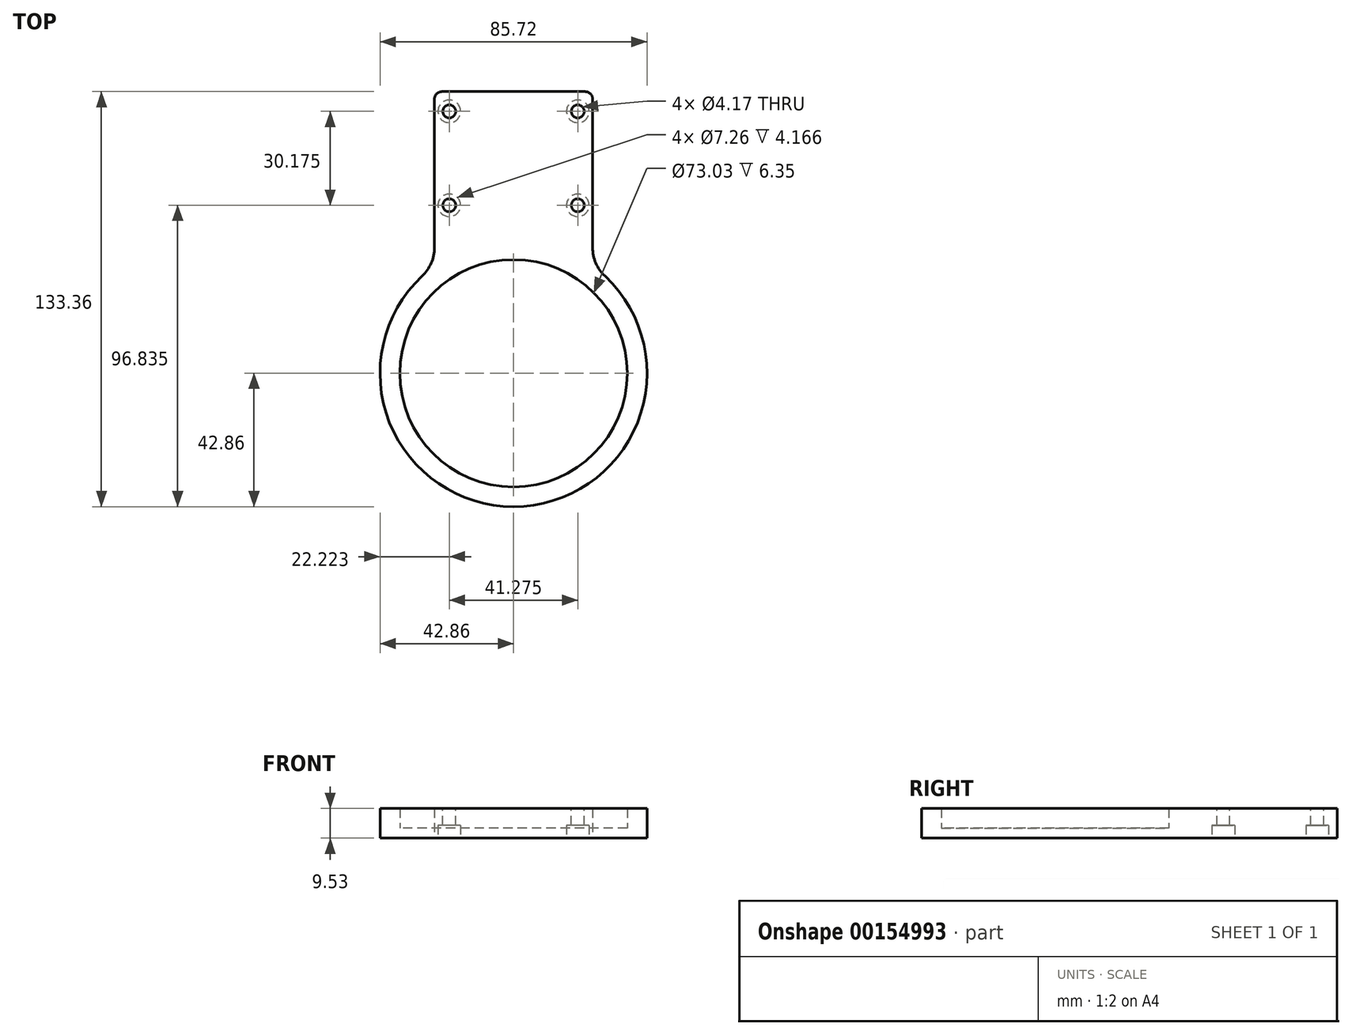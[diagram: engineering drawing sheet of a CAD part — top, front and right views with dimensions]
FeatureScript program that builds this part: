
annotation { "Feature Type Name" : "Feature", "Feature Type Description" : "" }
export const myFeature = defineFeature(function(context is Context, id is Id, definition is map)
    precondition{}
    {
        {
            var Q0;
            Q0=qCreatedBy(makeId("Top.planeOp"),FACE);
            var sketch = newSketch(context, id + "F0", { "sketchPlane" : qUnion([Q0])});
            skCircle(sketch, "E0", {"center": v(0, 0) * mm, "radius": 36.51 * mm});
            skArc(sketch, "E1", {"start": v(-25.4, 34.53) * mm, "mid": v(0, -42.86) * mm, "end": v(25.4, 34.53) * mm});
            skLineSegment(sketch, "E2", {"start": v(-25.4, 34.53) * mm, "end": v(-25.4, 90.5) * mm});
            skLineSegment(sketch, "E3", {"start": v(-25.4, 90.5) * mm, "end": v(25.4, 90.5) * mm});
            skLineSegment(sketch, "E4", {"start": v(25.4, 90.5) * mm, "end": v(25.4, 34.53) * mm});
            skLineSegment(sketch, "E5", {"start": v(0, 143.03) * mm, "end": v(0, 0) * mm, "construction": true});
            skSolve(sketch);
        }
        {
            var Q0;
            Q0=makeQuery(id+"F0.imprint","IMPRINT",FACE,{"disambiguationData":[TD([[makeQuery(id+"F0.imprint","IMPRINT",EDGE,{"derivedFrom":sQuery(id+"F0.wireOp",EDGE,"E0")}),-1.0]])]});
            extrude(context, id + "F1", {"entities" : qUnion([Q0]), "depth" : 9.52 * mm});
        }
        {
            var Q0;
            Q0=qCreatedBy(makeId("Top.planeOp"),FACE);
            var sketch = newSketch(context, id + "F2", { "sketchPlane" : qUnion([Q0])});
            skCircle(sketch, "E6", {"center": v(0, 0) * mm, "radius": 36.51 * mm});
            skSolve(sketch);
        }
        {
            var Q0;
            Q0 = qSketchRegion(id + "F2", true);
            extrude(context, id + "F3", {"entities" : qUnion([Q0]), "operationType" : NewBodyOperationType.ADD, "depth" : 3.17 * mm});
        }
        {
            var Q0;
            Q0=makeQuery(id+"F1.opExtrude","CAP_FACE",FACE,{"disambiguationData":[OSD([sQuery(id+"F0.wireOp",EDGE,"E0"),sQuery(id+"F0.wireOp",EDGE,"E1"),sQuery(id+"F0.wireOp",EDGE,"E2"),sQuery(id+"F0.wireOp",EDGE,"E3"),sQuery(id+"F0.wireOp",EDGE,"E4")])],"isStart":false});
            var sketch = newSketch(context, id + "F4", { "sketchPlane" : qUnion([Q0])});
            skLineSegment(sketch, "E7.bottom", {"start": v(-20.64, 84.15) * mm, "end": v(20.64, 84.15) * mm, "construction": true});
            skLineSegment(sketch, "E7.top", {"start": v(-20.64, 53.98) * mm, "end": v(20.64, 53.98) * mm, "construction": true});
            skLineSegment(sketch, "E7.left", {"start": v(-20.64, 84.15) * mm, "end": v(-20.64, 53.98) * mm, "construction": true});
            skLineSegment(sketch, "E7.right", {"start": v(20.64, 84.15) * mm, "end": v(20.64, 53.98) * mm, "construction": true});
            skCircle(sketch, "E8", {"center": v(-20.64, 84.15) * mm, "radius": 2.08 * mm});
            skCircle(sketch, "E9", {"center": v(20.64, 84.15) * mm, "radius": 2.08 * mm});
            skCircle(sketch, "E10", {"center": v(-20.64, 53.98) * mm, "radius": 2.08 * mm});
            skCircle(sketch, "E11", {"center": v(20.64, 53.98) * mm, "radius": 2.08 * mm});
            skSolve(sketch);
        }
        {
            var Q0;
            Q0 = qSketchRegion(id + "F4", true);
            extrude(context, id + "F5", {"entities" : qUnion([Q0]), "operationType" : NewBodyOperationType.REMOVE, "endBound" : BoundingType.THROUGH_ALL, "oppositeDirection" : true, "depth" : 25.4 * mm});
        }
        {
            var Q0;
            Q0=makeQuery(id+"F0.imprint","IMPRINT",FACE,{"disambiguationData":[TD([[makeQuery(id+"F0.imprint","IMPRINT",EDGE,{"derivedFrom":sQuery(id+"F0.wireOp",EDGE,"E0")}),-1.0]])]});
            var sketch = newSketch(context, id + "F6", { "sketchPlane" : qUnion([Q0])});
            skCircle(sketch, "E12.0", {"center": v(20.64, 84.15) * mm, "radius": 2.08 * mm});
            skCircle(sketch, "E12.1", {"center": v(20.64, 53.98) * mm, "radius": 2.08 * mm});
            skCircle(sketch, "E12.2", {"center": v(-20.64, 53.98) * mm, "radius": 2.08 * mm});
            skCircle(sketch, "E12.3", {"center": v(-20.64, 84.15) * mm, "radius": 2.08 * mm});
            skCircle(sketch, "E13", {"center": v(20.64, 84.15) * mm, "radius": 3.63 * mm});
            skCircle(sketch, "E14", {"center": v(-20.64, 84.15) * mm, "radius": 3.63 * mm});
            skCircle(sketch, "E15", {"center": v(-20.64, 53.98) * mm, "radius": 3.63 * mm});
            skCircle(sketch, "E16", {"center": v(20.64, 53.98) * mm, "radius": 3.63 * mm});
            skSolve(sketch);
        }
        {
            var Q0;
            Q0 = qSketchRegion(id + "F6", true);
            extrude(context, id + "F7", {"entities" : qUnion([Q0]), "operationType" : NewBodyOperationType.REMOVE, "depth" : 4.17 * mm});
        }
        {
            var Q0;
            Q0=makeQuery(id+"F1.opExtrude","SWEPT_EDGE",EDGE,{"disambiguationData":[OSD([sQuery(id+"F0.wireOp",EDGE,"E3"),sQuery(id+"F0.wireOp",EDGE,"E4")])]});
            var Q1;
            Q1=makeQuery(id+"F1.opExtrude","SWEPT_EDGE",EDGE,{"disambiguationData":[OSD([sQuery(id+"F0.wireOp",EDGE,"E2"),sQuery(id+"F0.wireOp",EDGE,"E3")])]});
            fillet(context, id + "F8", {"entities" : qUnion([Q0, Q1]), "radius" : 2.38 * mm, "tangentPropagation" : true, "allowEdgeOverflow" : false});
        }
        {
            var Q0;
            Q0=makeQuery(id+"F1.opExtrude","SWEPT_EDGE",EDGE,{"disambiguationData":[OSD([sQuery(id+"F0.wireOp",EDGE,"E1"),sQuery(id+"F0.wireOp",EDGE,"E4")])]});
            var Q1;
            Q1=makeQuery(id+"F1.opExtrude","SWEPT_EDGE",EDGE,{"disambiguationData":[OSD([sQuery(id+"F0.wireOp",EDGE,"E1"),sQuery(id+"F0.wireOp",EDGE,"E2")])]});
            fillet(context, id + "F9", {"entities" : qUnion([Q0, Q1]), "radius" : 12.7 * mm, "tangentPropagation" : true, "allowEdgeOverflow" : false});
        }
    });
